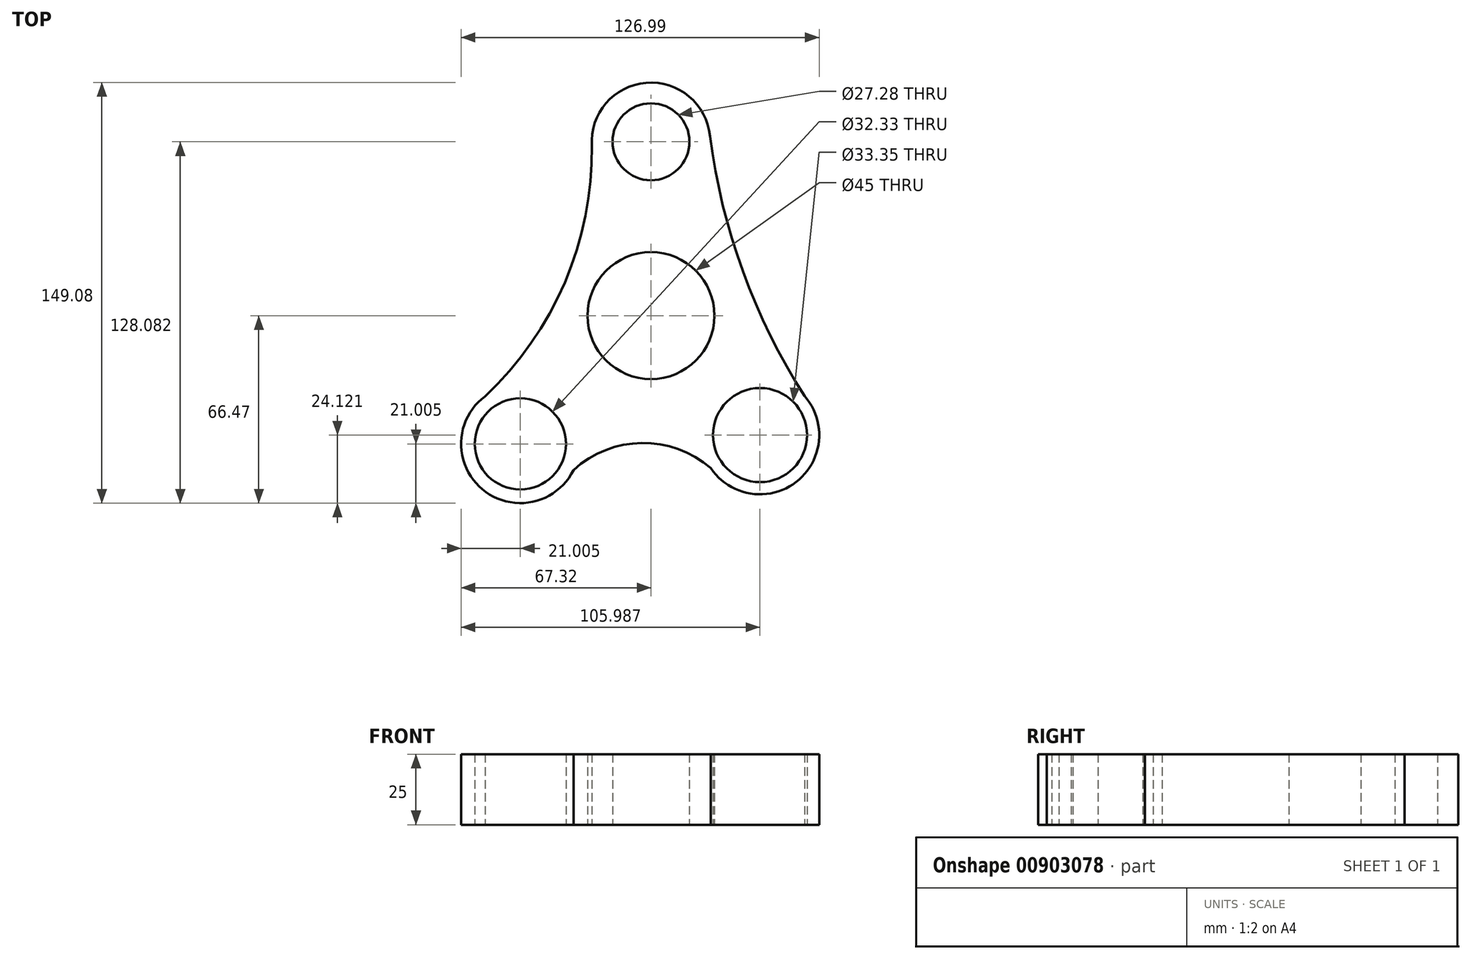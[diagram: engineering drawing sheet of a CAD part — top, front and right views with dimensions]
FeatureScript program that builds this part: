
annotation { "Feature Type Name" : "Feature", "Feature Type Description" : "" }
export const myFeature = defineFeature(function(context is Context, id is Id, definition is map)
    precondition{}
    {
        {
            var Q0;
            Q0=qCreatedBy(makeId("Top.planeOp"),FACE);
            var sketch = newSketch(context, id + "F0", { "sketchPlane" : qUnion([Q0])});
            skCircle(sketch, "E0", {"center": v(0, 0) * mm, "radius": 22.5 * mm});
            skArc(sketch, "E1", {"start": v(-58.8, -28.57) * mm, "mid": v(-59.79, -61.57) * mm, "end": v(-27.48, -54.76) * mm});
            skArc(sketch, "E2", {"start": v(21.25, -54.09) * mm, "mid": v(51.46, -59) * mm, "end": v(54.5, -28.55) * mm});
            skArc(sketch, "E3", {"start": v(20.9, 63.56) * mm, "mid": v(-1.72, 82.54) * mm, "end": v(-20.95, 60.13) * mm});
            skArc(sketch, "E4", {"start": v(21.25, -54.09) * mm, "mid": v(-3.24, -45.15) * mm, "end": v(-27.48, -54.76) * mm});
            skArc(sketch, "E5", {"start": v(-58.8, -28.57) * mm, "mid": v(-30.12, 12.77) * mm, "end": v(-21, 62.24) * mm});
            skArc(sketch, "E6", {"start": v(20.9, 63.56) * mm, "mid": v(32.62, 15.65) * mm, "end": v(54.5, -28.55) * mm});
            skCircle(sketch, "E7", {"center": v(0, 61.61) * mm, "radius": 13.64 * mm});
            skCircle(sketch, "E8", {"center": v(-46.32, -45.47) * mm, "radius": 16.16 * mm});
            skCircle(sketch, "E9", {"center": v(38.67, -42.35) * mm, "radius": 16.68 * mm});
            skSolve(sketch);
        }
        {
            var Q0;
            Q0 = qSketchRegion(id + "F0", true);
            extrude(context, id + "F1", {"entities" : qUnion([Q0]), "depth" : 25 * mm, "offsetDistance" : 25 * mm});
        }
    });
